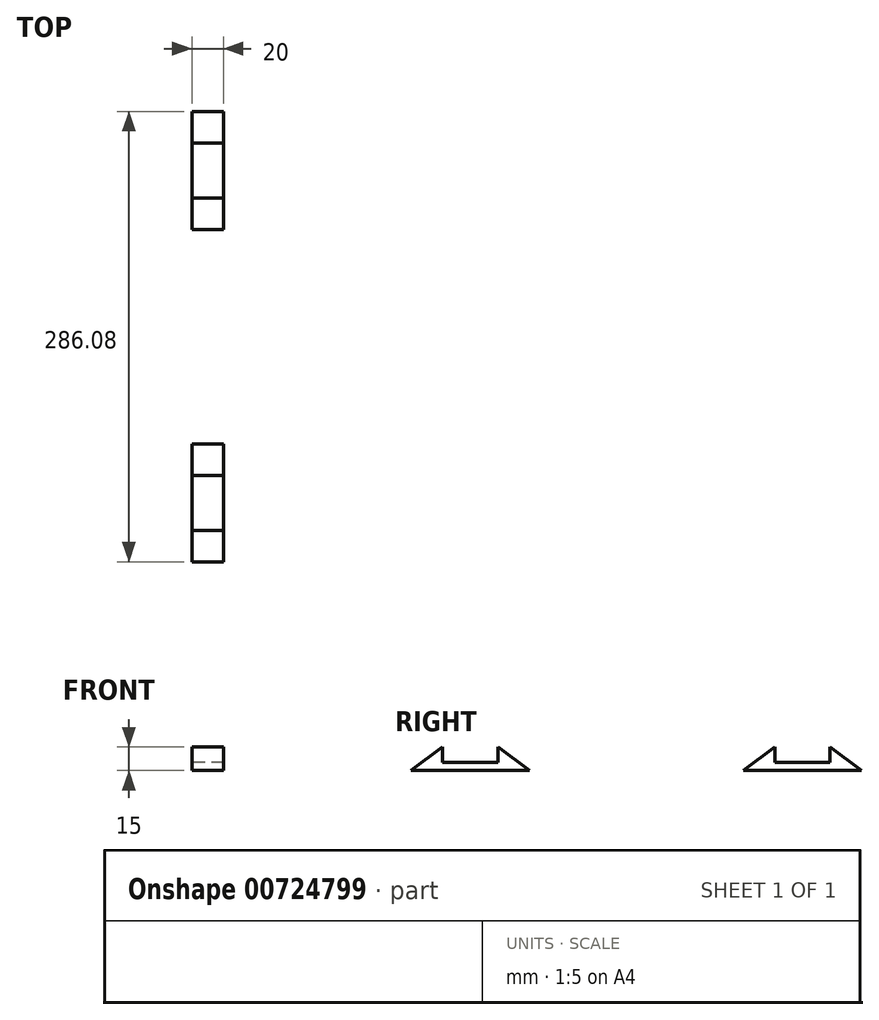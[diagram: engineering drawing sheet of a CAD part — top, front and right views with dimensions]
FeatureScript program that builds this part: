
annotation { "Feature Type Name" : "Feature", "Feature Type Description" : "" }
export const myFeature = defineFeature(function(context is Context, id is Id, definition is map)
    precondition{}
    {
        {
            var Q0;
            Q0=qCreatedBy(makeId("Right.planeOp"),FACE);
            var sketch = newSketch(context, id + "F0", { "sketchPlane" : qUnion([Q0])});
            skLineSegment(sketch, "E0", {"start": v(-68.04, 0) * mm, "end": v(-143.04, 0) * mm});
            skLineSegment(sketch, "E1", {"start": v(-143.04, 0) * mm, "end": v(-123.04, 15) * mm});
            skLineSegment(sketch, "E2", {"start": v(-123.04, 15) * mm, "end": v(-123.04, 5) * mm});
            skLineSegment(sketch, "E3", {"start": v(-123.04, 5) * mm, "end": v(-88.04, 5) * mm});
            skLineSegment(sketch, "E4", {"start": v(-88.04, 5) * mm, "end": v(-88.04, 15) * mm});
            skLineSegment(sketch, "E5", {"start": v(-88.04, 15) * mm, "end": v(-68.04, 0) * mm});
            skLineSegment(sketch, "E6", {"start": v(-105.54, 5) * mm, "end": v(-105.54, 0) * mm, "construction": true});
            skSolve(sketch);
        }
        {
            var Q0;
            Q0 = qSketchRegion(id + "F0", true);
            extrude(context, id + "F1", {"entities" : qUnion([Q0]), "depth" : 20 * mm, "offsetDistance" : 25 * mm});
        }
        {
            var Q0;
            Q0=makeQuery(id+"F1.opExtrude","SWEPT_BODY",BODY,{"disambiguationData":[OSD([sQuery(id+"F0.wireOp",EDGE,"E0"),sQuery(id+"F0.wireOp",EDGE,"E1"),sQuery(id+"F0.wireOp",EDGE,"E2"),sQuery(id+"F0.wireOp",EDGE,"E3"),sQuery(id+"F0.wireOp",EDGE,"E4"),sQuery(id+"F0.wireOp",EDGE,"E5")])]});
            var Q1;
            Q1=qCreatedBy(makeId("Front.planeOp"),FACE);
            mirror(context, id + "F2", {"entities" : qUnion([Q0]), "mirrorPlane" : qUnion([Q1])});
        }
    });
